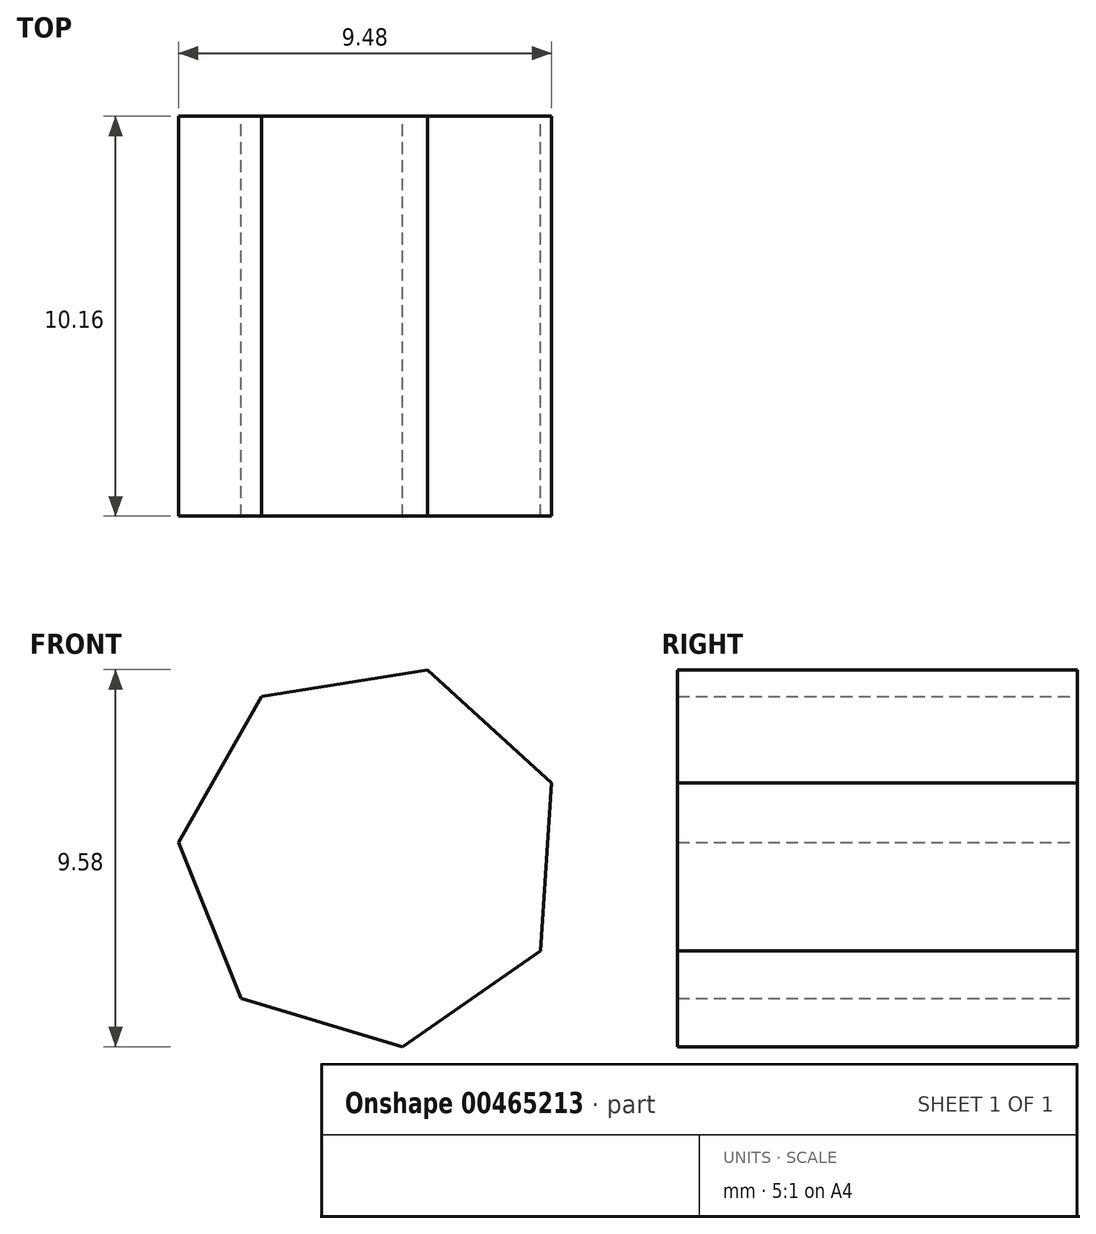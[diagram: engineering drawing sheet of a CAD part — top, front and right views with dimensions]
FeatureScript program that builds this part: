
annotation { "Feature Type Name" : "Feature", "Feature Type Description" : "" }
export const myFeature = defineFeature(function(context is Context, id is Id, definition is map)
    precondition{}
    {
        {
            var Q0;
            Q0=qCreatedBy(makeId("Front.planeOp"),FACE);
            var sketch = newSketch(context, id + "F0", { "sketchPlane" : qUnion([Q0])});
            skCircle(sketch, "E0.cCircle", {"center": v(0, 0) * mm, "radius": 4.44 * mm, "construction": true});
            skLineSegment(sketch, "E0.0", {"start": v(4.28, -2.42) * mm, "end": v(0.78, -4.86) * mm});
            skLineSegment(sketch, "E0.1", {"start": v(0.78, -4.86) * mm, "end": v(-3.32, -3.64) * mm});
            skLineSegment(sketch, "E0.2", {"start": v(-3.32, -3.64) * mm, "end": v(-4.91, 0.33) * mm});
            skLineSegment(sketch, "E0.3", {"start": v(-4.91, 0.33) * mm, "end": v(-2.8, 4.04) * mm});
            skLineSegment(sketch, "E0.4", {"start": v(-2.8, 4.04) * mm, "end": v(1.41, 4.72) * mm});
            skLineSegment(sketch, "E0.5", {"start": v(1.41, 4.72) * mm, "end": v(4.57, 1.84) * mm});
            skLineSegment(sketch, "E0.6", {"start": v(4.57, 1.84) * mm, "end": v(4.28, -2.42) * mm});
            skPoint(sketch, "E0.0.midPoint", {"position": v(2.53, -3.64) * mm});
            skSolve(sketch);
        }
        {
            var Q0;
            Q0=qSketchRegion(id+"F0",true);
            extrude(context, id + "F1", {"entities" : qUnion([Q0]), "depth" : 10.16 * mm});
        }
    });
